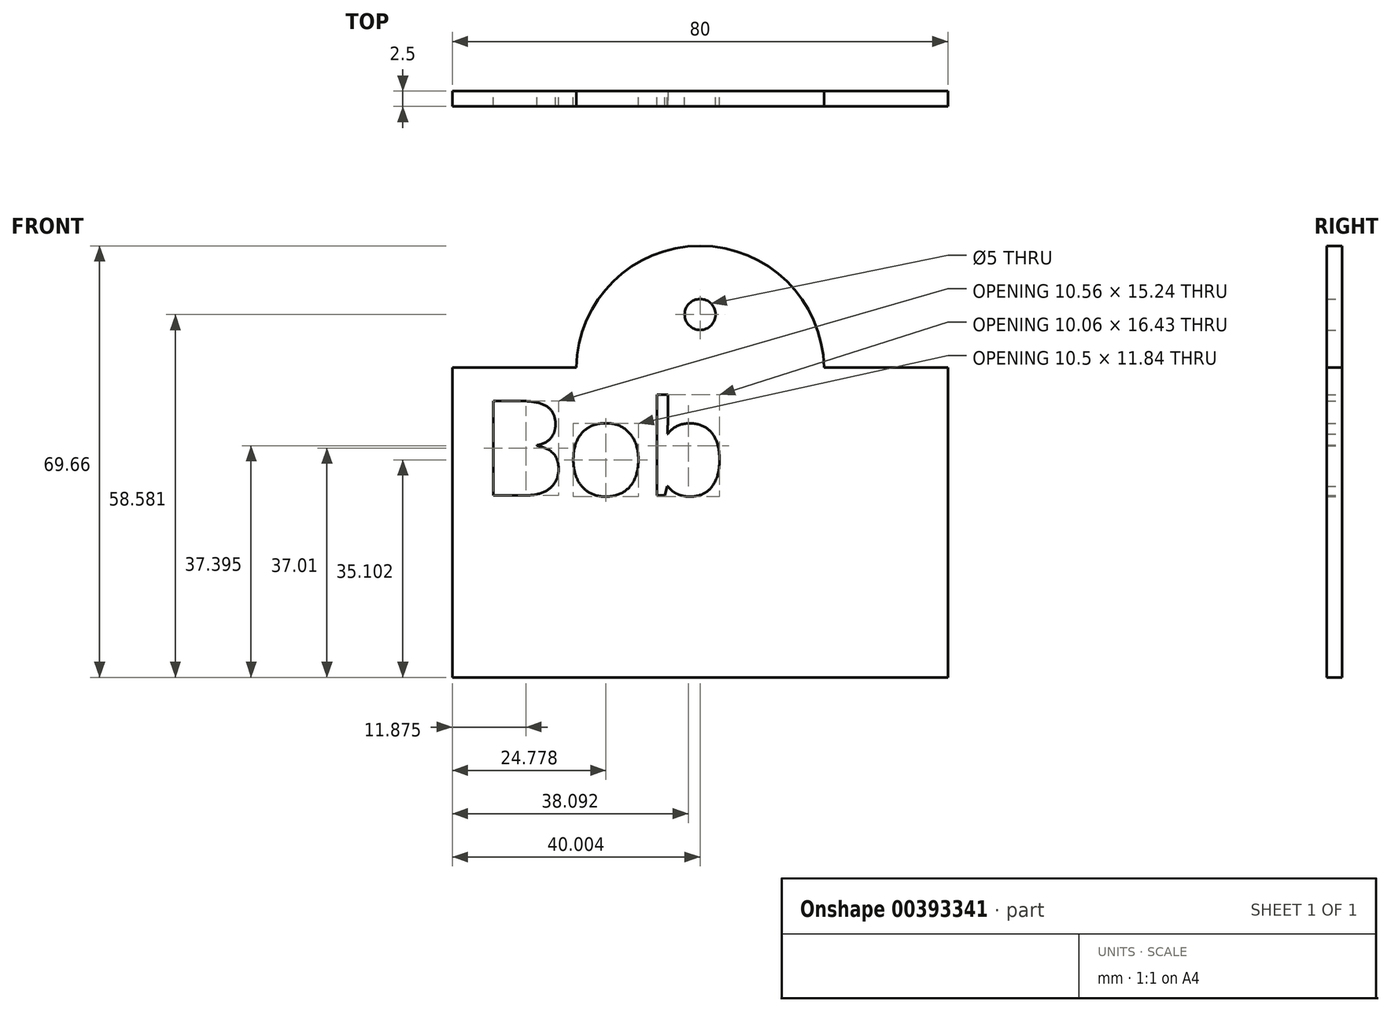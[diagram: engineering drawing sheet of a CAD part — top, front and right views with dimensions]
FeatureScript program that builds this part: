
annotation { "Feature Type Name" : "Feature", "Feature Type Description" : "" }
export const myFeature = defineFeature(function(context is Context, id is Id, definition is map)
    precondition{}
    {
        {
            var Q0;
            Q0=qCreatedBy(makeId("Front.planeOp"),FACE);
            var sketch = newSketch(context, id + "F0", { "sketchPlane" : qUnion([Q0])});
            skLineSegment(sketch, "E0.top", {"start": v(-39.02, -17.93) * mm, "end": v(40.98, -17.93) * mm});
            skLineSegment(sketch, "E0.left", {"start": v(-39.02, 32.07) * mm, "end": v(-39.02, -17.93) * mm});
            skLineSegment(sketch, "E0.right", {"start": v(40.98, 32.07) * mm, "end": v(40.98, -17.93) * mm});
            skPoint(sketch, "E1", {"position": v(0.98, 5.3) * mm});
            skPoint(sketch, "E1.positionSnap0", {"position": v(0.98, 32.07) * mm});
            skArc(sketch, "E2", {"start": v(20.98, 32.07) * mm, "mid": v(0.98, 51.73) * mm, "end": v(-19.02, 32.07) * mm});
            skLineSegment(sketch, "E3", {"start": v(-39.02, 32.07) * mm, "end": v(-19.02, 32.07) * mm});
            skLineSegment(sketch, "E4", {"start": v(20.98, 32.07) * mm, "end": v(40.98, 32.07) * mm});
            skCircle(sketch, "E5", {"center": v(0.98, 40.65) * mm, "radius": 2.5 * mm});
            skText(sketch, "E6", { "text": "Bob", "fontName": "OpenSans-Regular.ttf"});
            const initialGuessF0  = {"E6": [-0.03452, 0.01146, 1, 0, 0.01537]};
            skSetInitialGuess(sketch, initialGuessF0);
            skSolve(sketch);
        }
        {
            var Q0;
            Q0 = qSketchRegion(id + "F0", true);
            extrude(context, id + "F1", {"entities" : qUnion([Q0]), "depth" : 2.5 * mm});
        }
    });
